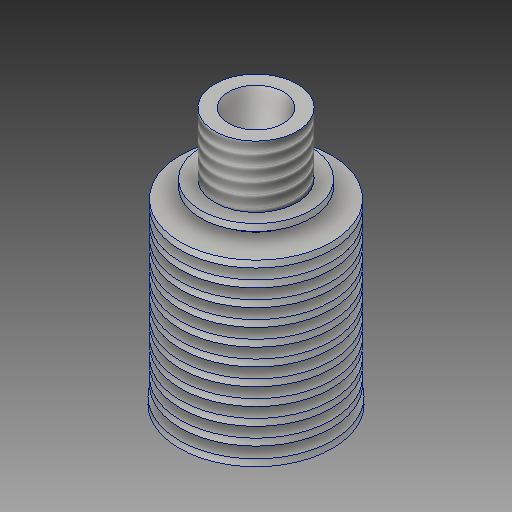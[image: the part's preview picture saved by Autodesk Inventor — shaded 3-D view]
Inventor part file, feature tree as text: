
AUTODESK INVENTOR PART (.ipt)
format: ipt  version: 2019 (Build 230136000, 136)  size: 287,744 bytes
history: native  units: mm
features: sketch x2, revolve x1, thread x1, extrude x1
ambient origin geometry x8: Origin, YZ Plane, XZ Plane, XY Plane, X Axis, Y Axis, Z Axis, Center Point
bodies: Solid1 (feature_tree)
feature tree (5):
  revolve  "Revolution1"  [1 undecoded]
  thread  "Thread1"  [1 undecoded]
  extrude  "Extrusion1"  Depth=3.0mm
  sketch  "Sketch1"  dims[d5=1.0mm d6=1.5mm d7=11.0mm]
  sketch  "Sketch2"  dims[d8=11.15mm d9=3.0mm d10=15.1mm d11=2.1mm d12=37.5mm d13=26.0mm d14=28.5mm d16=8.0mm d17=6.0mm d18=21.25mm d19=90.0deg d20=10.0mm d21=0.0mm d22=8.0mm d23=6.0mm d24=0.0mm]
note: 2 required parameter values undecoded (feature->parameter linkage not recoverable at this tier; creation-order binding heuristic only, values carry confidence <= 0.55)